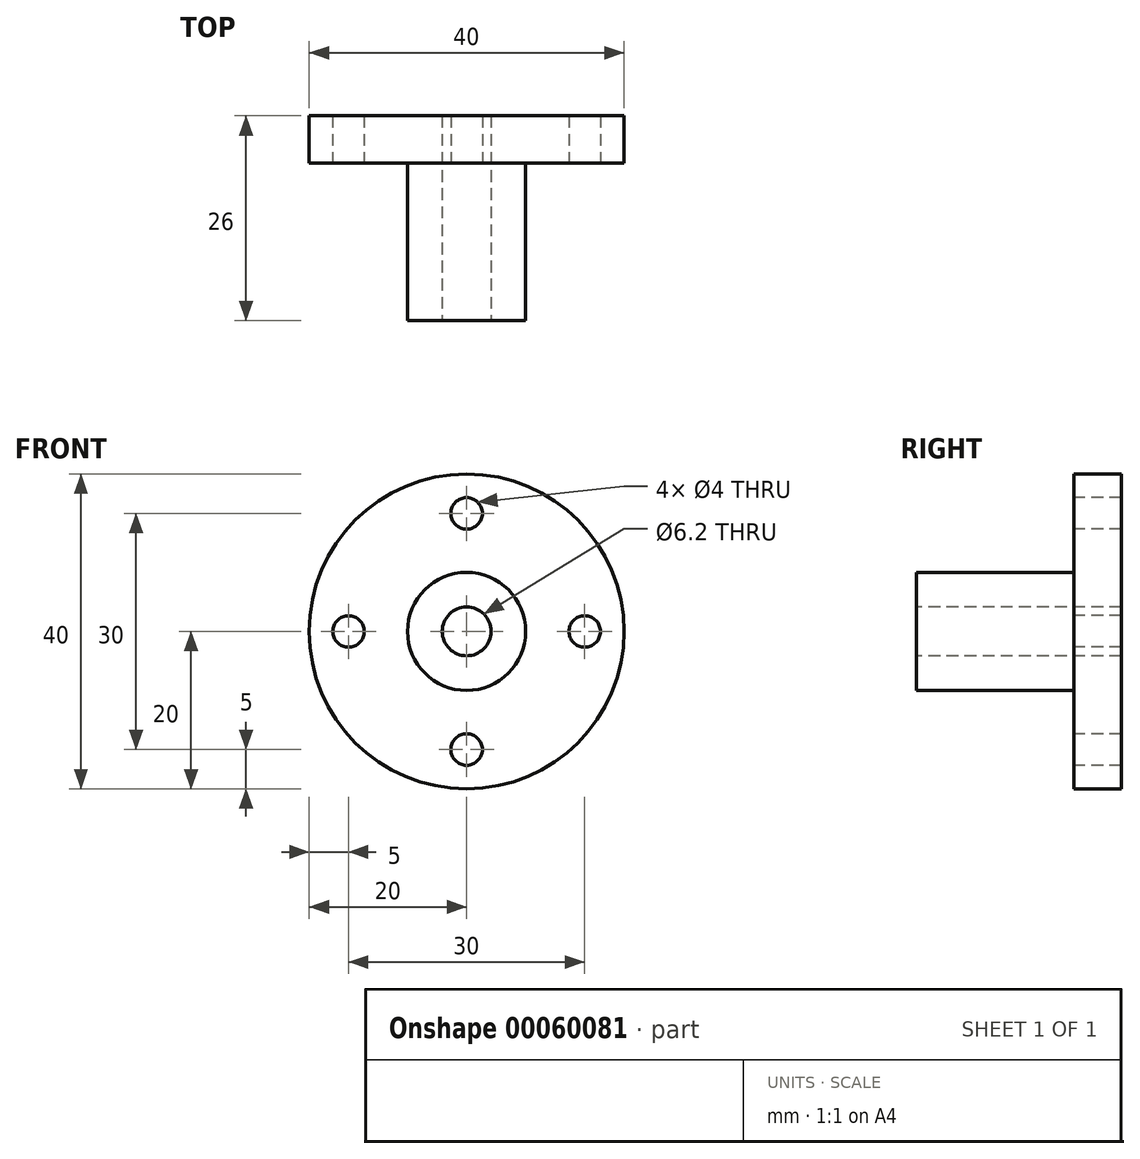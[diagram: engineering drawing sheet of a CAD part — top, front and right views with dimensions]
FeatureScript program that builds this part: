
annotation { "Feature Type Name" : "Feature", "Feature Type Description" : "" }
export const myFeature = defineFeature(function(context is Context, id is Id, definition is map)
    precondition{}
    {
        {
            var Q0;
            Q0=qCreatedBy(makeId("Front.planeOp"),FACE);
            var sketch = newSketch(context, id + "F0", { "sketchPlane" : qUnion([Q0])});
            skCircle(sketch, "E0", {"center": v(0, 0) * mm, "radius": 20 * mm});
            skSolve(sketch);
        }
        {
            var Q0;
            Q0 = qSketchRegion(id + "F0", true);
            extrude(context, id + "F1", {"entities" : qUnion([Q0]), "depth" : 6 * mm});
        }
        {
            var Q0;
            Q0=makeQuery(id+"F1.opExtrude","CAP_FACE",FACE,{"disambiguationData":[OSD([sQuery(id+"F0.wireOp",EDGE,"E0")])],"isStart":false});
            var sketch = newSketch(context, id + "F2", { "sketchPlane" : qUnion([Q0])});
            skCircle(sketch, "E1", {"center": v(0, 0) * mm, "radius": 7.5 * mm});
            skSolve(sketch);
        }
        {
            var Q0;
            Q0 = qSketchRegion(id + "F2", true);
            extrude(context, id + "F3", {"entities" : qUnion([Q0]), "operationType" : NewBodyOperationType.ADD, "depth" : 20 * mm});
        }
        {
            var Q0;
            Q0=makeQuery(id+"F3.opExtrude","CAP_FACE",FACE,{"disambiguationData":[OSD([sQuery(id+"F2.wireOp",EDGE,"E1")])],"isStart":false});
            var sketch = newSketch(context, id + "F4", { "sketchPlane" : qUnion([Q0])});
            skCircle(sketch, "E2", {"center": v(0, 0) * mm, "radius": 3.1 * mm});
            skSolve(sketch);
        }
        {
            var Q0;
            Q0 = qSketchRegion(id + "F4", true);
            extrude(context, id + "F5", {"entities" : qUnion([Q0]), "operationType" : NewBodyOperationType.REMOVE, "endBound" : BoundingType.THROUGH_ALL, "oppositeDirection" : true, "depth" : 25 * mm});
        }
        {
            var Q0;
            Q0=makeQuery(id+"F1.opExtrude","CAP_FACE",FACE,{"disambiguationData":[OSD([sQuery(id+"F0.wireOp",EDGE,"E0")])],"isStart":false});
            var sketch = newSketch(context, id + "F6", { "sketchPlane" : qUnion([Q0])});
            skCircle(sketch, "E3", {"center": v(0, 15) * mm, "radius": 2 * mm});
            skCircle(sketch, "E4", {"center": v(0, -15) * mm, "radius": 2 * mm});
            skCircle(sketch, "E5", {"center": v(15, 0) * mm, "radius": 2 * mm});
            skCircle(sketch, "E6", {"center": v(-15, 0) * mm, "radius": 2 * mm});
            skSolve(sketch);
        }
        {
            var Q0;
            Q0 = qSketchRegion(id + "F6", true);
            extrude(context, id + "F7", {"entities" : qUnion([Q0]), "operationType" : NewBodyOperationType.REMOVE, "endBound" : BoundingType.THROUGH_ALL, "oppositeDirection" : true, "depth" : 25 * mm});
        }
    });
